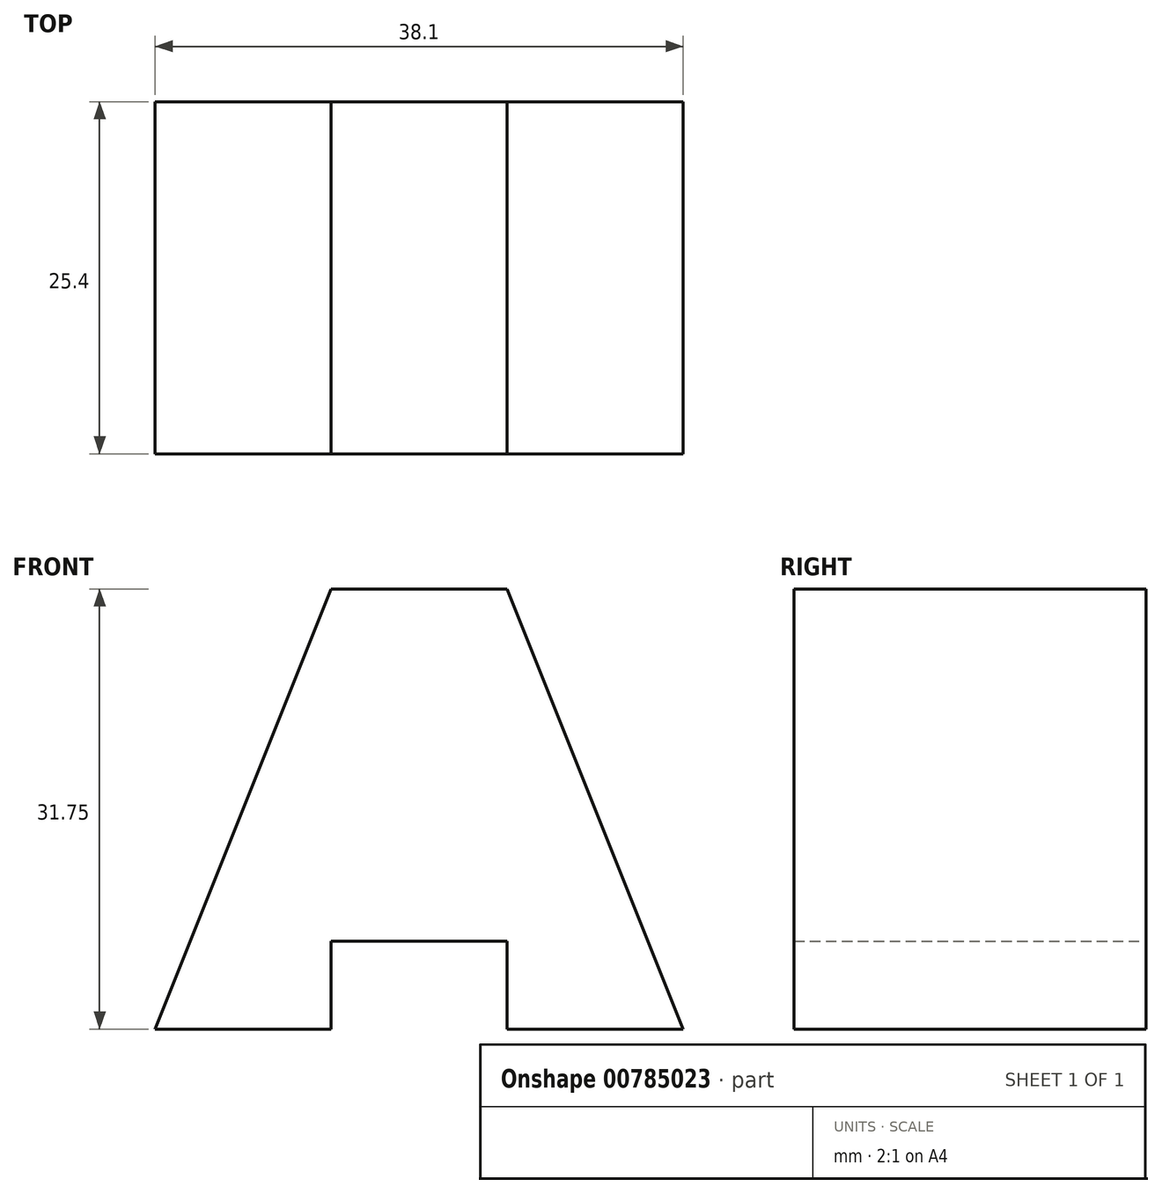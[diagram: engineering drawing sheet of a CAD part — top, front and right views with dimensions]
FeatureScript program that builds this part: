
annotation { "Feature Type Name" : "Feature", "Feature Type Description" : "" }
export const myFeature = defineFeature(function(context is Context, id is Id, definition is map)
    precondition{}
    {
        {
            var Q0;
            Q0=qCreatedBy(makeId("Front.planeOp"),FACE);
            var sketch = newSketch(context, id + "F0", { "sketchPlane" : qUnion([Q0])});
            skLineSegment(sketch, "E0", {"start": v(0, 0) * mm, "end": v(38.1, 0) * mm});
            skLineSegment(sketch, "E1", {"start": v(0, 0) * mm, "end": v(0, 31.75) * mm});
            skLineSegment(sketch, "E2", {"start": v(38.1, 0) * mm, "end": v(38.1, 31.75) * mm});
            skLineSegment(sketch, "E3", {"start": v(38.1, 31.75) * mm, "end": v(0, 31.75) * mm});
            skSolve(sketch);
        }
        {
            var Q0;
            Q0=makeQuery(id+"F0.imprint","IMPRINT",FACE,{"disambiguationData":[TD([[makeQuery(id+"F0.imprint","IMPRINT",EDGE,{"derivedFrom":sQuery(id+"F0.wireOp",EDGE,"E0")}),1.0]])]});
            extrude(context, id + "F1", {"entities" : qUnion([Q0]), "depth" : 25.4 * mm, "offsetDistance" : 25.4 * mm});
        }
        {
            var Q0;
            Q0=makeQuery(id+"F1.opExtrude","CAP_FACE",FACE,{"disambiguationData":[OSD([sQuery(id+"F0.wireOp",EDGE,"E0"),sQuery(id+"F0.wireOp",EDGE,"E1"),sQuery(id+"F0.wireOp",EDGE,"E2"),sQuery(id+"F0.wireOp",EDGE,"E3")])],"isStart":true});
            var sketch = newSketch(context, id + "F2", { "sketchPlane" : qUnion([Q0])});
            skLineSegment(sketch, "E4", {"start": v(0, 0) * mm, "end": v(-12.7, 0) * mm});
            skLineSegment(sketch, "E5", {"start": v(-12.7, 0) * mm, "end": v(-12.7, 6.35) * mm});
            skLineSegment(sketch, "E6", {"start": v(-12.7, 6.35) * mm, "end": v(-25.4, 6.35) * mm});
            skLineSegment(sketch, "E7", {"start": v(-25.4, 6.35) * mm, "end": v(-25.4, 0) * mm});
            skSolve(sketch);
        }
        {
            var Q0;
            {var subQ0=sQuery(id+"F2.wireOp",EDGE,"E5");Q0=makeQuery(id+"F2.imprint","IMPRINT",FACE,{"disambiguationData":[TD([[makeQuery(id+"F2.imprint","IMPRINT",EDGE,{"derivedFrom":subQ0}),1.0]])]});}
            extrude(context, id + "F3", {"entities" : qUnion([Q0]), "operationType" : NewBodyOperationType.REMOVE, "oppositeDirection" : true, "depth" : 25.4 * mm, "offsetDistance" : 25.4 * mm});
        }
        {
            var Q0;
            Q0=makeQuery(id+"F1.opExtrude","CAP_FACE",FACE,{"disambiguationData":[OSD([sQuery(id+"F0.wireOp",EDGE,"E0"),sQuery(id+"F0.wireOp",EDGE,"E1"),sQuery(id+"F0.wireOp",EDGE,"E2"),sQuery(id+"F0.wireOp",EDGE,"E3")])],"isStart":true});
            var sketch = newSketch(context, id + "F4", { "sketchPlane" : qUnion([Q0])});
            skLineSegment(sketch, "E8", {"start": v(0, 31.75) * mm, "end": v(-12.7, 31.75) * mm});
            skLineSegment(sketch, "E9", {"start": v(-12.7, 31.75) * mm, "end": v(-25.4, 31.75) * mm});
            skLineSegment(sketch, "E10", {"start": v(-12.7, 31.75) * mm, "end": v(0, 0) * mm});
            skLineSegment(sketch, "E11", {"start": v(-25.4, 31.75) * mm, "end": v(-38.1, 0) * mm});
            skSolve(sketch);
        }
        {
            var Q0;
            {var subQ0=sQuery(id+"F4.wireOp",EDGE,"E11");Q0=makeQuery(id+"F4.imprint","IMPRINT",FACE,{"disambiguationData":[TD([[makeQuery(id+"F4.imprint","IMPRINT",EDGE,{"derivedFrom":subQ0}),-1.0]])]});}
            extrude(context, id + "F5", {"entities" : qUnion([Q0]), "operationType" : NewBodyOperationType.REMOVE, "oppositeDirection" : true, "depth" : 25.4 * mm, "offsetDistance" : 25.4 * mm});
        }
        {
            var Q0;
            Q0=makeQuery(id+"F1.opExtrude","CAP_FACE",FACE,{"disambiguationData":[OSD([sQuery(id+"F0.wireOp",EDGE,"E0"),sQuery(id+"F0.wireOp",EDGE,"E1"),sQuery(id+"F0.wireOp",EDGE,"E2"),sQuery(id+"F0.wireOp",EDGE,"E3")])],"isStart":true});
            var sketch = newSketch(context, id + "F6", { "sketchPlane" : qUnion([Q0])});
            skLineSegment(sketch, "E12", {"start": v(0, 31.75) * mm, "end": v(-12.7, 31.75) * mm});
            skLineSegment(sketch, "E13", {"start": v(-12.7, 31.75) * mm, "end": v(0, 0) * mm});
            skSolve(sketch);
        }
        {
            var Q0;
            Q0=makeQuery(id+"F6.imprint","IMPRINT",FACE,{"disambiguationData":[TD([[makeQuery(id+"F6.imprint","IMPRINT",EDGE,{"derivedFrom":sQuery(id+"F6.wireOp",EDGE,"E12")}),-1.0]])]});
            extrude(context, id + "F7", {"entities" : qUnion([Q0]), "operationType" : NewBodyOperationType.REMOVE, "oppositeDirection" : true, "depth" : 25.4 * mm, "offsetDistance" : 25.4 * mm});
        }
    });
